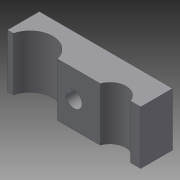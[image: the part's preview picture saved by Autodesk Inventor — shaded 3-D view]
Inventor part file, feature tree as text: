
AUTODESK INVENTOR PART (.ipt)
format: ipt  version: 2014 (Build 180170000, 170)  size: 90,624 bytes
history: native  units: mm
features: sketch x2, other x1, extrude x1, hole x1
ambient origin geometry x8: Origin, YZ Plane, XZ Plane, XY Plane, X Axis, Y Axis, Z Axis, Center Point
bodies: Body1 (feature_tree)
feature tree (5):
  other  "Твердое тело1"
  extrude  "Выдавливание1"  Depth=25.0mm
  hole  "Отверстие1"  [1 undecoded]
  sketch  "Эскиз1"
  sketch  "Эскиз2"
note: 1 required parameter value undecoded (feature->parameter linkage not recoverable at this tier; creation-order binding heuristic only, values carry confidence <= 0.55)
